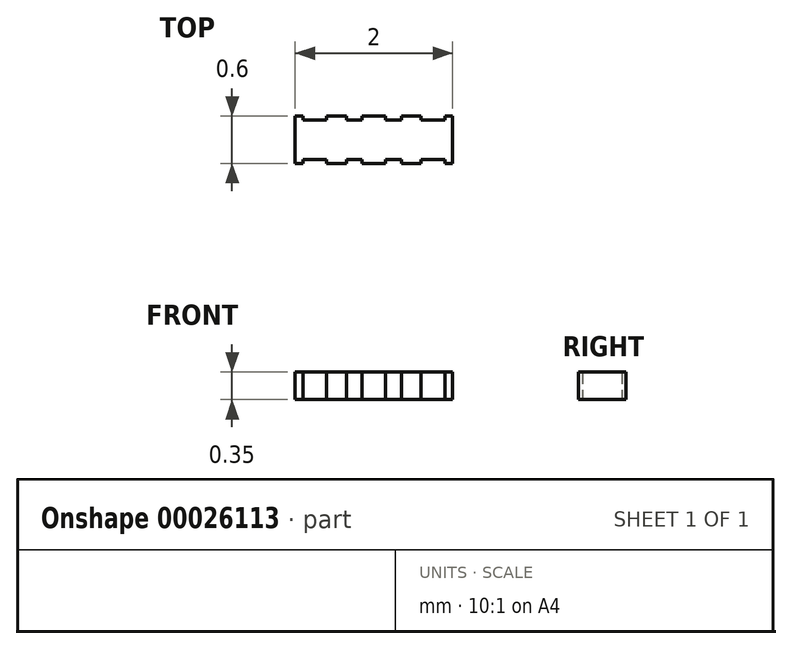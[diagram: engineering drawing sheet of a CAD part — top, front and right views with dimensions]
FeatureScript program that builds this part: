
annotation { "Feature Type Name" : "Feature", "Feature Type Description" : "" }
export const myFeature = defineFeature(function(context is Context, id is Id, definition is map)
    precondition{}
    {
        {
            var Q0;
            Q0=qCreatedBy(makeId("Top.planeOp"),FACE);
            var sketch = newSketch(context, id + "F0", { "sketchPlane" : qUnion([Q0])});
            skLineSegment(sketch, "E0.rect.bottom", {"start": v(1, -0.3) * mm, "end": v(-1, -0.3) * mm});
            skLineSegment(sketch, "E0.rect.top", {"start": v(1, 0.3) * mm, "end": v(-1, 0.3) * mm});
            skLineSegment(sketch, "E0.rect.left", {"start": v(1, -0.3) * mm, "end": v(1, 0.3) * mm});
            skLineSegment(sketch, "E0.rect.right", {"start": v(-1, -0.3) * mm, "end": v(-1, 0.3) * mm});
            skPoint(sketch, "E0.rect.middle", {"position": v(0, 0) * mm});
            skSolve(sketch);
        }
        {
            var Q0;
            Q0=makeQuery(id+"F0.imprint","IMPRINT",FACE,{"disambiguationData":[TD([[makeQuery(id+"F0.imprint","IMPRINT",EDGE,{"derivedFrom":sQuery(id+"F0.wireOp",EDGE,"E0.rect.bottom")}),-1.0]])]});
            extrude(context, id + "F1", {"entities" : qUnion([Q0]), "depth" : 0.35 * mm});
        }
        {
            var Q0;
            Q0=qCreatedBy(makeId("Top.planeOp"),FACE);
            var sketch = newSketch(context, id + "F2", { "sketchPlane" : qUnion([Q0])});
            skLineSegment(sketch, "E1.rect.bottom", {"start": v(-0.6, -0.5) * mm, "end": v(-0.9, -0.5) * mm});
            skLineSegment(sketch, "E1.rect.top", {"start": v(-0.6, -0.25) * mm, "end": v(-0.9, -0.25) * mm});
            skLineSegment(sketch, "E1.rect.left", {"start": v(-0.6, -0.5) * mm, "end": v(-0.6, -0.25) * mm});
            skLineSegment(sketch, "E1.rect.right", {"start": v(-0.9, -0.5) * mm, "end": v(-0.9, -0.25) * mm});
            skPoint(sketch, "E1.rect.middle", {"position": v(-0.75, -0.38) * mm});
            skLineSegment(sketch, "E2.MirrorCS", {"start": v(0.9, -0.5) * mm, "end": v(0.9, -0.25) * mm});
            skLineSegment(sketch, "E3.MirrorCS", {"start": v(0.6, -0.25) * mm, "end": v(0.9, -0.25) * mm});
            skLineSegment(sketch, "E4.MirrorCS", {"start": v(0.6, -0.5) * mm, "end": v(0.9, -0.5) * mm});
            skLineSegment(sketch, "E5.MirrorCS", {"start": v(0.6, -0.5) * mm, "end": v(0.6, -0.25) * mm});
            skLineSegment(sketch, "E6.MirrorCS", {"start": v(0.6, 0.25) * mm, "end": v(0.9, 0.25) * mm});
            skLineSegment(sketch, "E7.MirrorCS", {"start": v(0.6, 0.5) * mm, "end": v(0.6, 0.25) * mm});
            skLineSegment(sketch, "E8.MirrorCS", {"start": v(0.9, 0.5) * mm, "end": v(0.9, 0.25) * mm});
            skLineSegment(sketch, "E9.MirrorCS", {"start": v(0.6, 0.5) * mm, "end": v(0.9, 0.5) * mm});
            skLineSegment(sketch, "E10.MirrorCS", {"start": v(-0.9, 0.5) * mm, "end": v(-0.9, 0.25) * mm});
            skLineSegment(sketch, "E11.MirrorCS", {"start": v(-0.6, 0.25) * mm, "end": v(-0.9, 0.25) * mm});
            skLineSegment(sketch, "E12.MirrorCS", {"start": v(-0.6, 0.5) * mm, "end": v(-0.6, 0.25) * mm});
            skLineSegment(sketch, "E13.MirrorCS", {"start": v(-0.6, 0.5) * mm, "end": v(-0.9, 0.5) * mm});
            skLineSegment(sketch, "E14.rect.bottom", {"start": v(-0.15, 0.25) * mm, "end": v(-0.35, 0.25) * mm});
            skLineSegment(sketch, "E14.rect.top", {"start": v(-0.15, 0.5) * mm, "end": v(-0.35, 0.5) * mm});
            skLineSegment(sketch, "E14.rect.left", {"start": v(-0.15, 0.25) * mm, "end": v(-0.15, 0.5) * mm});
            skLineSegment(sketch, "E14.rect.right", {"start": v(-0.35, 0.25) * mm, "end": v(-0.35, 0.5) * mm});
            skPoint(sketch, "E14.rect.middle", {"position": v(-0.25, 0.38) * mm});
            skLineSegment(sketch, "E15.MirrorCS", {"start": v(0.15, 0.25) * mm, "end": v(0.15, 0.5) * mm});
            skLineSegment(sketch, "E16.MirrorCS", {"start": v(0.15, 0.5) * mm, "end": v(0.35, 0.5) * mm});
            skLineSegment(sketch, "E17.MirrorCS", {"start": v(0.35, 0.25) * mm, "end": v(0.35, 0.5) * mm});
            skLineSegment(sketch, "E18.MirrorCS", {"start": v(0.15, 0.25) * mm, "end": v(0.35, 0.25) * mm});
            skLineSegment(sketch, "E19.MirrorCS", {"start": v(-0.35, -0.25) * mm, "end": v(-0.35, -0.5) * mm});
            skLineSegment(sketch, "E20.MirrorCS", {"start": v(-0.15, -0.25) * mm, "end": v(-0.35, -0.25) * mm});
            skLineSegment(sketch, "E21.MirrorCS", {"start": v(-0.15, -0.25) * mm, "end": v(-0.15, -0.5) * mm});
            skLineSegment(sketch, "E22.MirrorCS", {"start": v(-0.15, -0.5) * mm, "end": v(-0.35, -0.5) * mm});
            skLineSegment(sketch, "E23.MirrorCS", {"start": v(0.15, -0.5) * mm, "end": v(0.35, -0.5) * mm});
            skLineSegment(sketch, "E24.MirrorCS", {"start": v(0.15, -0.25) * mm, "end": v(0.15, -0.5) * mm});
            skLineSegment(sketch, "E25.MirrorCS", {"start": v(0.15, -0.25) * mm, "end": v(0.35, -0.25) * mm});
            skLineSegment(sketch, "E26.MirrorCS", {"start": v(0.35, -0.25) * mm, "end": v(0.35, -0.5) * mm});
            skSolve(sketch);
        }
        {
            var Q0;
            Q0=qSketchRegion(id+"F2",true);
            extrude(context, id + "F3", {"entities" : qUnion([Q0]), "depth" : 0.35 * mm});
        }
        {
            var Q0;
            Q0=makeQuery(id+"F3.opExtrude","CAP_EDGE",EDGE,{"disambiguationData":[OSD([sQuery(id+"F2.wireOp",EDGE,"E9.MirrorCS")])],"isStart":false});
            var Q1;
            Q1=makeQuery(id+"F3.opExtrude","CAP_EDGE",EDGE,{"disambiguationData":[OSD([sQuery(id+"F2.wireOp",EDGE,"E16.MirrorCS")])],"isStart":false});
            var Q2;
            Q2=makeQuery(id+"F3.opExtrude","CAP_EDGE",EDGE,{"disambiguationData":[OSD([sQuery(id+"F2.wireOp",EDGE,"E14.rect.top")])],"isStart":false});
            var Q3;
            Q3=makeQuery(id+"F3.opExtrude","CAP_EDGE",EDGE,{"disambiguationData":[OSD([sQuery(id+"F2.wireOp",EDGE,"E13.MirrorCS")])],"isStart":false});
            var Q4;
            Q4=makeQuery(id+"F3.opExtrude","CAP_EDGE",EDGE,{"disambiguationData":[OSD([sQuery(id+"F2.wireOp",EDGE,"E4.MirrorCS")])],"isStart":false});
            var Q5;
            Q5=makeQuery(id+"F3.opExtrude","CAP_EDGE",EDGE,{"disambiguationData":[OSD([sQuery(id+"F2.wireOp",EDGE,"E23.MirrorCS")])],"isStart":false});
            var Q6;
            Q6=makeQuery(id+"F3.opExtrude","CAP_EDGE",EDGE,{"disambiguationData":[OSD([sQuery(id+"F2.wireOp",EDGE,"E22.MirrorCS")])],"isStart":false});
            var Q7;
            Q7=makeQuery(id+"F3.opExtrude","CAP_EDGE",EDGE,{"disambiguationData":[OSD([sQuery(id+"F2.wireOp",EDGE,"E1.rect.bottom")])],"isStart":false});
            fillet(context, id + "F4", {"entities" : qUnion([Q0, Q1, Q2, Q3, Q4, Q5, Q6, Q7]), "radius" : 0.1 * mm, "tangentPropagation" : true, "allowEdgeOverflow" : false});
        }
        {
            var Q0;
            Q0=makeQuery(id+"F3.opExtrude","SWEPT_BODY",BODY,{"disambiguationData":[OSD([sQuery(id+"F2.wireOp",EDGE,"E1.rect.bottom"),sQuery(id+"F2.wireOp",EDGE,"E1.rect.top"),sQuery(id+"F2.wireOp",EDGE,"E1.rect.left"),sQuery(id+"F2.wireOp",EDGE,"E1.rect.right")])]});
            var Q1;
            Q1=makeQuery(id+"F1.opExtrude","SWEPT_BODY",BODY,{"disambiguationData":[OSD([sQuery(id+"F0.wireOp",EDGE,"E0.rect.bottom"),sQuery(id+"F0.wireOp",EDGE,"E0.rect.top"),sQuery(id+"F0.wireOp",EDGE,"E0.rect.left"),sQuery(id+"F0.wireOp",EDGE,"E0.rect.right")])]});
            booleanBodies(context, id + "F5", {"operationType" : BooleanOperationType.SUBTRACTION, "tools" : qUnion([Q0]), "targets" : qUnion([Q1]), "keepTools" : true});
        }
        {
            var Q0;
            Q0=makeQuery(id+"F3.opExtrude","SWEPT_BODY",BODY,{"disambiguationData":[OSD([sQuery(id+"F2.wireOp",EDGE,"E2.MirrorCS"),sQuery(id+"F2.wireOp",EDGE,"E3.MirrorCS"),sQuery(id+"F2.wireOp",EDGE,"E4.MirrorCS"),sQuery(id+"F2.wireOp",EDGE,"E5.MirrorCS")])]});
            var Q1;
            Q1=makeQuery(id+"F3.opExtrude","SWEPT_BODY",BODY,{"disambiguationData":[OSD([sQuery(id+"F2.wireOp",EDGE,"E6.MirrorCS"),sQuery(id+"F2.wireOp",EDGE,"E7.MirrorCS"),sQuery(id+"F2.wireOp",EDGE,"E8.MirrorCS"),sQuery(id+"F2.wireOp",EDGE,"E9.MirrorCS")])]});
            var Q2;
            Q2=makeQuery(id+"F3.opExtrude","SWEPT_BODY",BODY,{"disambiguationData":[OSD([sQuery(id+"F2.wireOp",EDGE,"E10.MirrorCS"),sQuery(id+"F2.wireOp",EDGE,"E11.MirrorCS"),sQuery(id+"F2.wireOp",EDGE,"E12.MirrorCS"),sQuery(id+"F2.wireOp",EDGE,"E13.MirrorCS")])]});
            var Q3;
            Q3=makeQuery(id+"F3.opExtrude","SWEPT_BODY",BODY,{"disambiguationData":[OSD([sQuery(id+"F2.wireOp",EDGE,"E14.rect.bottom"),sQuery(id+"F2.wireOp",EDGE,"E14.rect.top"),sQuery(id+"F2.wireOp",EDGE,"E14.rect.left"),sQuery(id+"F2.wireOp",EDGE,"E14.rect.right")])]});
            var Q4;
            Q4=makeQuery(id+"F3.opExtrude","SWEPT_BODY",BODY,{"disambiguationData":[OSD([sQuery(id+"F2.wireOp",EDGE,"E15.MirrorCS"),sQuery(id+"F2.wireOp",EDGE,"E16.MirrorCS"),sQuery(id+"F2.wireOp",EDGE,"E17.MirrorCS"),sQuery(id+"F2.wireOp",EDGE,"E18.MirrorCS")])]});
            var Q5;
            Q5=makeQuery(id+"F3.opExtrude","SWEPT_BODY",BODY,{"disambiguationData":[OSD([sQuery(id+"F2.wireOp",EDGE,"E19.MirrorCS"),sQuery(id+"F2.wireOp",EDGE,"E20.MirrorCS"),sQuery(id+"F2.wireOp",EDGE,"E21.MirrorCS"),sQuery(id+"F2.wireOp",EDGE,"E22.MirrorCS")])]});
            var Q6;
            Q6=makeQuery(id+"F3.opExtrude","SWEPT_BODY",BODY,{"disambiguationData":[OSD([sQuery(id+"F2.wireOp",EDGE,"E23.MirrorCS"),sQuery(id+"F2.wireOp",EDGE,"E24.MirrorCS"),sQuery(id+"F2.wireOp",EDGE,"E25.MirrorCS"),sQuery(id+"F2.wireOp",EDGE,"E26.MirrorCS")])]});
            var Q7;
            Q7=makeQuery(id+"F1.opExtrude","SWEPT_BODY",BODY,{"disambiguationData":[OSD([sQuery(id+"F0.wireOp",EDGE,"E0.rect.bottom"),sQuery(id+"F0.wireOp",EDGE,"E0.rect.top"),sQuery(id+"F0.wireOp",EDGE,"E0.rect.left"),sQuery(id+"F0.wireOp",EDGE,"E0.rect.right")])]});
            booleanBodies(context, id + "F6", {"operationType" : BooleanOperationType.SUBTRACTION, "tools" : qUnion([Q0, Q1, Q2, Q3, Q4, Q5, Q6]), "targets" : qUnion([Q7]), "keepTools" : true});
        }
        {
            var Q0;
            Q0=makeQuery(id+"F3.opExtrude","SWEPT_BODY",BODY,{"disambiguationData":[OSD([sQuery(id+"F2.wireOp",EDGE,"E1.rect.bottom"),sQuery(id+"F2.wireOp",EDGE,"E1.rect.top"),sQuery(id+"F2.wireOp",EDGE,"E1.rect.left"),sQuery(id+"F2.wireOp",EDGE,"E1.rect.right")])]});
            var Q1;
            Q1=makeQuery(id+"F3.opExtrude","SWEPT_BODY",BODY,{"disambiguationData":[OSD([sQuery(id+"F2.wireOp",EDGE,"E2.MirrorCS"),sQuery(id+"F2.wireOp",EDGE,"E3.MirrorCS"),sQuery(id+"F2.wireOp",EDGE,"E4.MirrorCS"),sQuery(id+"F2.wireOp",EDGE,"E5.MirrorCS")])]});
            var Q2;
            Q2=makeQuery(id+"F3.opExtrude","SWEPT_BODY",BODY,{"disambiguationData":[OSD([sQuery(id+"F2.wireOp",EDGE,"E6.MirrorCS"),sQuery(id+"F2.wireOp",EDGE,"E7.MirrorCS"),sQuery(id+"F2.wireOp",EDGE,"E8.MirrorCS"),sQuery(id+"F2.wireOp",EDGE,"E9.MirrorCS")])]});
            var Q3;
            Q3=makeQuery(id+"F3.opExtrude","SWEPT_BODY",BODY,{"disambiguationData":[OSD([sQuery(id+"F2.wireOp",EDGE,"E10.MirrorCS"),sQuery(id+"F2.wireOp",EDGE,"E11.MirrorCS"),sQuery(id+"F2.wireOp",EDGE,"E12.MirrorCS"),sQuery(id+"F2.wireOp",EDGE,"E13.MirrorCS")])]});
            var Q4;
            Q4=makeQuery(id+"F3.opExtrude","SWEPT_BODY",BODY,{"disambiguationData":[OSD([sQuery(id+"F2.wireOp",EDGE,"E14.rect.bottom"),sQuery(id+"F2.wireOp",EDGE,"E14.rect.top"),sQuery(id+"F2.wireOp",EDGE,"E14.rect.left"),sQuery(id+"F2.wireOp",EDGE,"E14.rect.right")])]});
            var Q5;
            Q5=makeQuery(id+"F3.opExtrude","SWEPT_BODY",BODY,{"disambiguationData":[OSD([sQuery(id+"F2.wireOp",EDGE,"E15.MirrorCS"),sQuery(id+"F2.wireOp",EDGE,"E16.MirrorCS"),sQuery(id+"F2.wireOp",EDGE,"E17.MirrorCS"),sQuery(id+"F2.wireOp",EDGE,"E18.MirrorCS")])]});
            var Q6;
            Q6=makeQuery(id+"F3.opExtrude","SWEPT_BODY",BODY,{"disambiguationData":[OSD([sQuery(id+"F2.wireOp",EDGE,"E19.MirrorCS"),sQuery(id+"F2.wireOp",EDGE,"E20.MirrorCS"),sQuery(id+"F2.wireOp",EDGE,"E21.MirrorCS"),sQuery(id+"F2.wireOp",EDGE,"E22.MirrorCS")])]});
            var Q7;
            Q7=makeQuery(id+"F3.opExtrude","SWEPT_BODY",BODY,{"disambiguationData":[OSD([sQuery(id+"F2.wireOp",EDGE,"E23.MirrorCS"),sQuery(id+"F2.wireOp",EDGE,"E24.MirrorCS"),sQuery(id+"F2.wireOp",EDGE,"E25.MirrorCS"),sQuery(id+"F2.wireOp",EDGE,"E26.MirrorCS")])]});
            deleteBodies(context, id + "F7", {"entities" : qUnion([Q0, Q1, Q2, Q3, Q4, Q5, Q6, Q7])});
        }
    });
